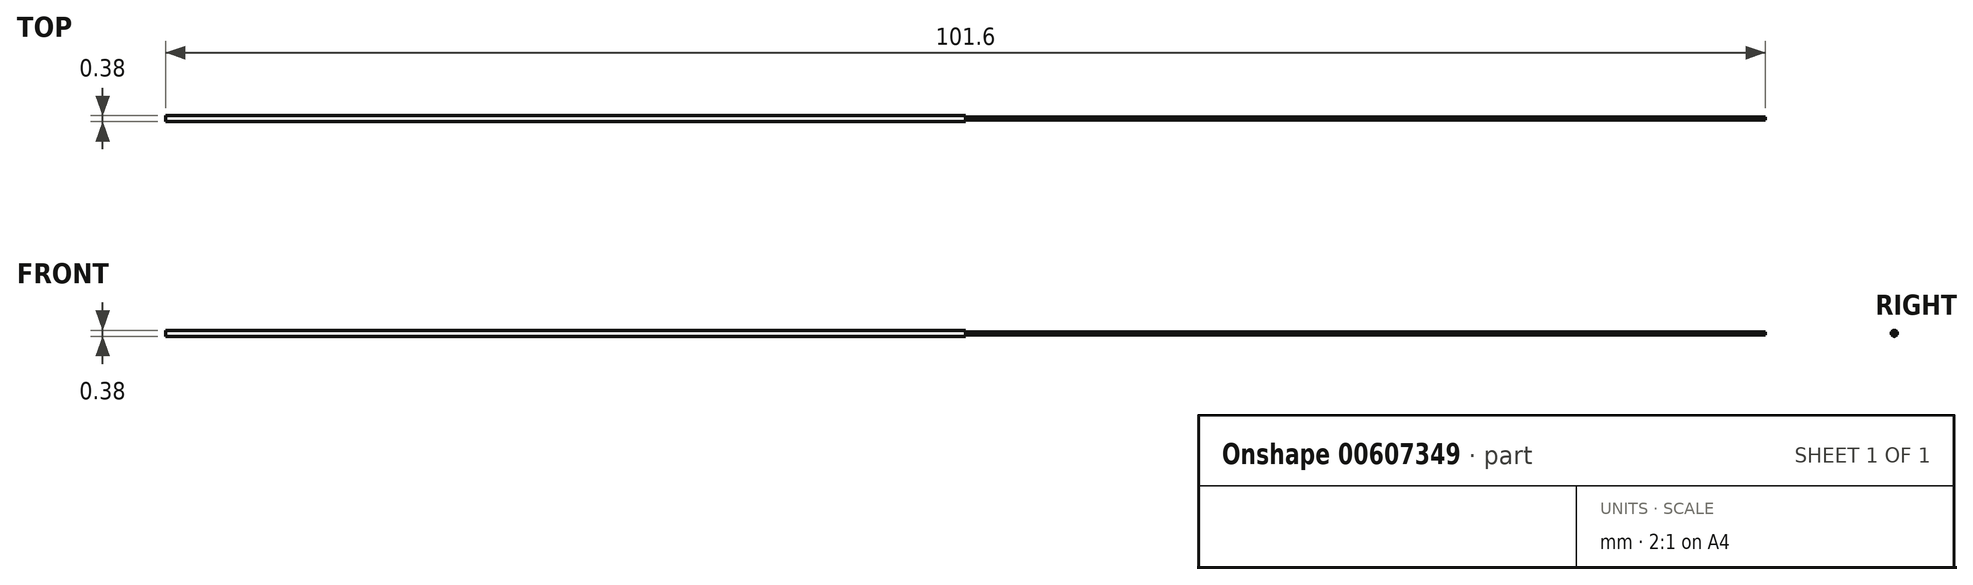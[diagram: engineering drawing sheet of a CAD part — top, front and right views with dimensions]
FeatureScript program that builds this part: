
annotation { "Feature Type Name" : "Feature", "Feature Type Description" : "" }
export const myFeature = defineFeature(function(context is Context, id is Id, definition is map)
    precondition{}
    {
        {
            var Q0;
            Q0=qCreatedBy(makeId("Front.planeOp"),FACE);
            var sketch = newSketch(context, id + "F0", { "sketchPlane" : qUnion([Q0])});
            skLineSegment(sketch, "E0.bottom", {"start": v(-50.8, 0.2) * mm, "end": v(0, 0.2) * mm});
            skLineSegment(sketch, "E0.top", {"start": v(-50.8, 0) * mm, "end": v(0, 0) * mm});
            skLineSegment(sketch, "E0.left", {"start": v(-50.8, 0.2) * mm, "end": v(-50.8, 0) * mm});
            skLineSegment(sketch, "E0.right", {"start": v(0, 0.2) * mm, "end": v(0, 0) * mm});
            skLineSegment(sketch, "E1.bottom", {"start": v(50.8, 0) * mm, "end": v(0, 0) * mm});
            skLineSegment(sketch, "E1.top", {"start": v(50.8, 0.1) * mm, "end": v(0, 0.1) * mm});
            skLineSegment(sketch, "E1.left", {"start": v(50.8, 0) * mm, "end": v(50.8, 0.1) * mm});
            skLineSegment(sketch, "E1.right", {"start": v(0, 0) * mm, "end": v(0, 0.1) * mm});
            skSolve(sketch);
        }
        {
            var Q0;
            Q0 = qSketchRegion(id + "F0", true);
            var Q1;
            Q1=sQuery(id+"F0.wireOp",EDGE,"E0.top");
            revolve(context, id + "F1", {"entities" : qUnion([Q0]), "axis" : qUnion([Q1]), "revolveType" : RevolveType.FULL});
        }
    });
